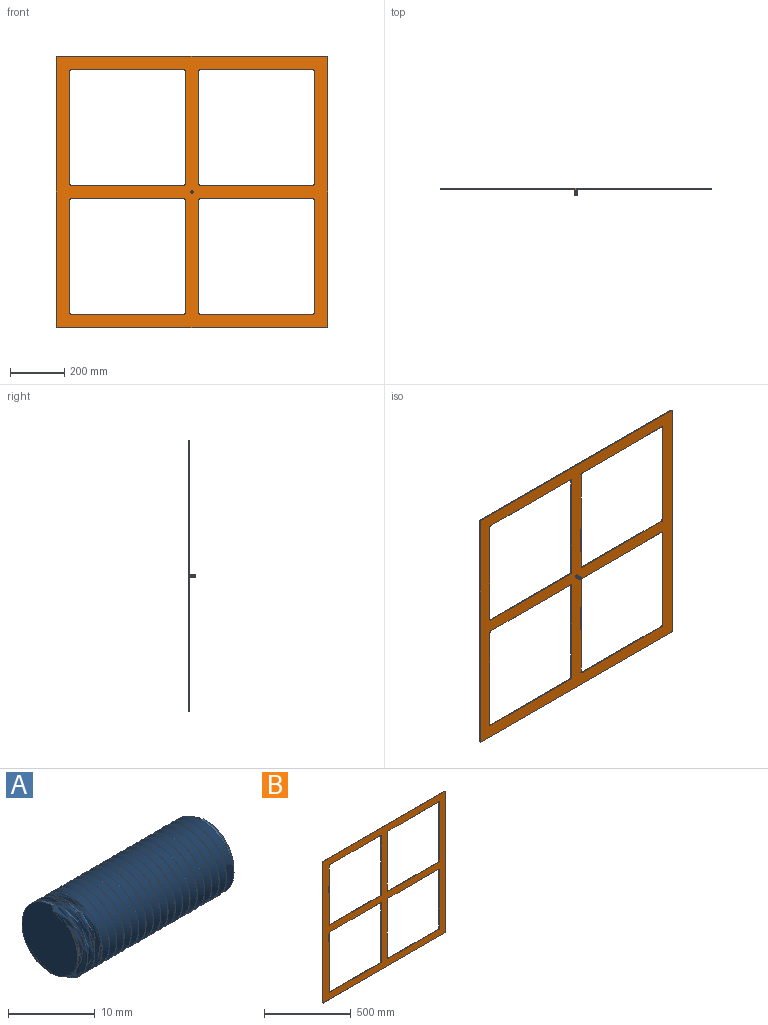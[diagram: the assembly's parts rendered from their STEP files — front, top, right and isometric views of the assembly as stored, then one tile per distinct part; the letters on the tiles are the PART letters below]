
ASSEMBLY  parts=2 mates=1
PART A: 8 faces, bbox 26.7x12.3x10.7 mm
  f0: plane 10.38x9.87mm, normal (-1,0,0), area 67mm2, adj f1,f4,f5,f6
  f1: cylinder r=5mm len=24.5mm, axis (-1,0,0), area 13.7mm2, adj f0,f3,f4,f5,f6,f7
  f2: plane 9.03x9.03mm, normal (1,0,0), area 63.6mm2, adj f3,f6,f7
  f3: cone r=4.5mm half-angle=45deg, axis (-1,0,0), area 13mm2, adj f1,f2,f6,f7
  f4: plane 0.6x0.34mm, normal (0,-1,0), area 0.1mm2, adj f0,f1,f6
  f5: bspline ~25.38x11.55mm, area 670.6mm2, adj f0,f1,f6,f7
  f6: bspline ~25.58x11.55mm, area 673.8mm2, adj f0,f1,f2,f3,f4,f5,f7
  f7: plane 1x0.81mm, normal (0,1,0), area 0.3mm2, adj f1,f2,f3,f5,f6
PART B: 42 faces, bbox 1000x3x1000 mm
  f0: plane 990x3mm, normal (0,0,-1), area 2970mm2, adj f1,f39,f40,f41
  f1: cylinder r=5mm len=5mm, axis (0,1,0), area 23.6mm2, adj f0,f2,f40,f41
  f2: plane 990x3mm, normal (1,0,0), area 2970mm2, adj f1,f3,f40,f41
  f3: cylinder r=5mm len=5mm, axis (0,1,0), area 23.6mm2, adj f2,f4,f40,f41
  f4: plane 990x3mm, normal (0,0,1), area 2970mm2, adj f3,f5,f40,f41
  f5: cylinder r=5mm len=5mm, axis (0,1,0), area 23.6mm2, adj f4,f6,f40,f41
  f6: plane 990x3mm, normal (-1,0,0), area 2970mm2, adj f5,f39,f40,f41
  f7: plane 415x3mm, normal (0,0,-1), area 1245mm2, adj f8,f35,f40,f41
  f8: cylinder r=5mm len=5mm, axis (0,1,0), area 23.6mm2, adj f7,f9,f40,f41
  f9: plane 415x3mm, normal (-1,0,0), area 1245mm2, adj f8,f10,f40,f41
  f10: cylinder r=5mm len=5mm, axis (0,1,0), area 23.6mm2, adj f9,f11,f40,f41
  f11: plane 415x3mm, normal (0,0,1), area 1245mm2, adj f10,f12,f40,f41
  f12: cylinder r=5mm len=5mm, axis (0,1,0), area 23.6mm2, adj f11,f13,f40,f41
  f13: plane 415x3mm, normal (1,0,0), area 1245mm2, adj f12,f35,f40,f41
  f14: plane 415x3mm, normal (-1,0,0), area 1245mm2, adj f15,f36,f40,f41
  f15: cylinder r=5mm len=5mm, axis (0,1,0), area 23.6mm2, adj f14,f16,f40,f41
  f16: plane 415x3mm, normal (0,0,1), area 1245mm2, adj f15,f17,f40,f41
  f17: cylinder r=5mm len=5mm, axis (0,1,0), area 23.6mm2, adj f16,f18,f40,f41
  f18: plane 415x3mm, normal (1,0,0), area 1245mm2, adj f17,f19,f40,f41
  f19: cylinder r=5mm len=5mm, axis (0,1,0), area 23.6mm2, adj f18,f20,f40,f41
  f20: plane 415x3mm, normal (0,0,-1), area 1245mm2, adj f19,f36,f40,f41
  f21: plane 415x3mm, normal (-1,0,0), area 1245mm2, adj f22,f37,f40,f41
  f22: cylinder r=5mm len=5mm, axis (0,1,0), area 23.6mm2, adj f21,f23,f40,f41
  f23: plane 415x3mm, normal (0,0,1), area 1245mm2, adj f22,f24,f40,f41
  f24: cylinder r=5mm len=5mm, axis (0,1,0), area 23.6mm2, adj f23,f25,f40,f41
  f25: plane 415x3mm, normal (1,0,0), area 1245mm2, adj f24,f26,f40,f41
  f26: cylinder r=5mm len=5mm, axis (0,1,0), area 23.6mm2, adj f25,f27,f40,f41
  f27: plane 415x3mm, normal (0,0,-1), area 1245mm2, adj f26,f37,f40,f41
  f28: plane 415x3mm, normal (-1,0,0), area 1245mm2, adj f29,f38,f40,f41
  f29: cylinder r=5mm len=5mm, axis (0,1,0), area 23.6mm2, adj f28,f30,f40,f41
  f30: plane 415x3mm, normal (0,0,1), area 1245mm2, adj f29,f31,f40,f41
  f31: cylinder r=5mm len=5mm, axis (0,1,0), area 23.6mm2, adj f30,f32,f40,f41
  f32: plane 415x3mm, normal (1,0,0), area 1245mm2, adj f31,f33,f40,f41
  f33: cylinder r=5mm len=5mm, axis (0,1,0), area 23.6mm2, adj f32,f34,f40,f41
  f34: plane 415x3mm, normal (0,0,-1), area 1245mm2, adj f33,f38,f40,f41
  f35: cylinder r=5mm len=5mm, axis (0,1,0), area 23.6mm2, adj f7,f13,f40,f41
  f36: cylinder r=5mm len=5mm, axis (0,1,0), area 23.6mm2, adj f14,f20,f40,f41
  f37: cylinder r=5mm len=5mm, axis (0,1,0), area 23.6mm2, adj f21,f27,f40,f41
  f38: cylinder r=5mm len=5mm, axis (0,1,0), area 23.6mm2, adj f28,f34,f40,f41
  f39: cylinder r=5mm len=5mm, axis (0,1,0), area 23.6mm2, adj f0,f6,f40,f41
  f40: plane 1000x1000mm, normal (0,-1,0), area 277564.4mm2, adj f0,f1,f2,f3,f4,f5,f6,f7
  f41: plane 1000x1000mm, normal (0,1,0), area 277564.4mm2, adj f0,f1,f2,f3,f4,f5,f6,f7
PLACE A rot(axis=(0.58,-0.58,-0.58),120deg) t=(-4.82,0.28,2.35)mm
PLACE B t=(-4.82,0.28,2.35)mm
MATE planar A.f1 <-> B.f41  axis (0,1,0) through (-4.82,0.28,2.35)mm
